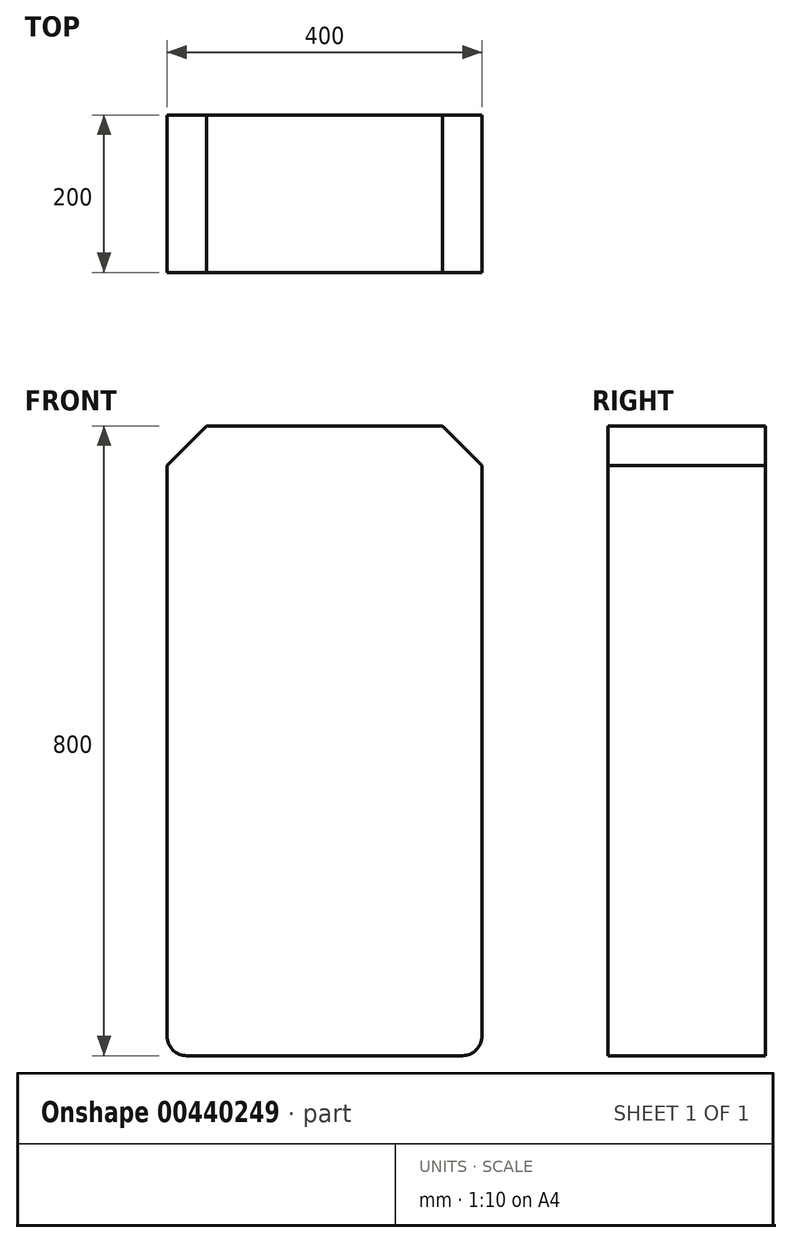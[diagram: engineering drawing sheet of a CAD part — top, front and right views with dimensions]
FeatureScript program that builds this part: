
annotation { "Feature Type Name" : "Feature", "Feature Type Description" : "" }
export const myFeature = defineFeature(function(context is Context, id is Id, definition is map)
    precondition{}
    {
        {
            var Q0;
            Q0=qCreatedBy(makeId("Front.planeOp"),FACE);
            var sketch = newSketch(context, id + "F0", { "sketchPlane" : qUnion([Q0])});
            skLineSegment(sketch, "E0.bottom", {"start": v(0, 0) * mm, "end": v(-400, 0) * mm});
            skLineSegment(sketch, "E0.top", {"start": v(0, 800) * mm, "end": v(-400, 800) * mm});
            skLineSegment(sketch, "E0.left", {"start": v(0, 0) * mm, "end": v(0, 800) * mm});
            skLineSegment(sketch, "E0.right", {"start": v(-400, 0) * mm, "end": v(-400, 800) * mm});
            skSolve(sketch);
        }
        {
            var Q0;
            Q0 = qSketchRegion(id + "F0", true);
            extrude(context, id + "F1", {"entities" : qUnion([Q0]), "depth" : 200 * mm});
        }
        {
            var Q0;
            Q0=makeQuery(id+"F1.opExtrude","SWEPT_EDGE",EDGE,{"disambiguationData":[OSD([sQuery(id+"F0.wireOp",EDGE,"E0.bottom"),sQuery(id+"F0.wireOp",EDGE,"E0.left")])]});
            var Q1;
            Q1=makeQuery(id+"F1.opExtrude","SWEPT_EDGE",EDGE,{"disambiguationData":[OSD([sQuery(id+"F0.wireOp",EDGE,"E0.bottom"),sQuery(id+"F0.wireOp",EDGE,"E0.right")])]});
            fillet(context, id + "F2", {"entities" : qUnion([Q0, Q1]), "radius" : 25 * mm, "tangentPropagation" : true, "allowEdgeOverflow" : false});
        }
        {
            var Q0;
            Q0=makeQuery(id+"F1.opExtrude","SWEPT_EDGE",EDGE,{"disambiguationData":[OSD([sQuery(id+"F0.wireOp",EDGE,"E0.top"),sQuery(id+"F0.wireOp",EDGE,"E0.right")])]});
            chamfer(context, id + "F3", {"entities" : qUnion([Q0]), "width" : 50 * mm, "tangentPropagation" : true});
        }
        {
            var Q0;
            Q0=makeQuery(id+"F1.opExtrude","SWEPT_EDGE",EDGE,{"disambiguationData":[OSD([sQuery(id+"F0.wireOp",EDGE,"E0.top"),sQuery(id+"F0.wireOp",EDGE,"E0.left")])]});
            chamfer(context, id + "F4", {"entities" : qUnion([Q0]), "width" : 50 * mm, "tangentPropagation" : true});
        }
    });
